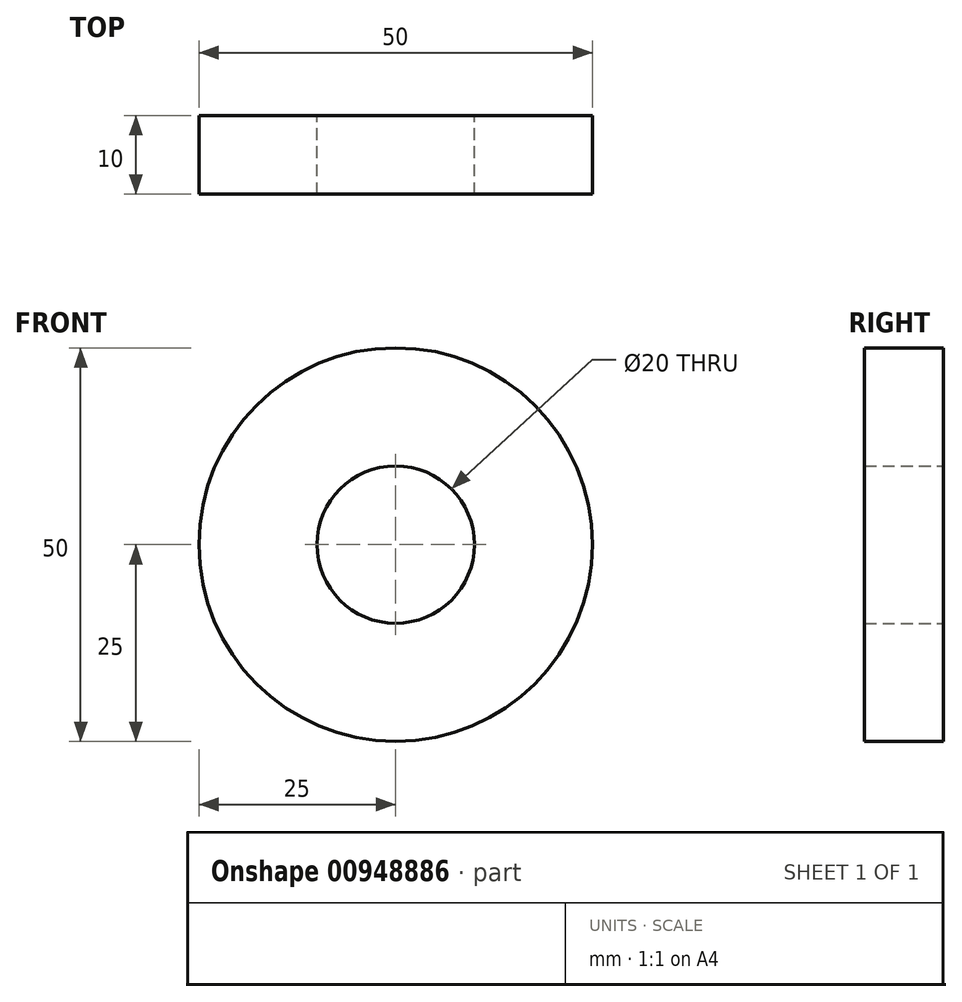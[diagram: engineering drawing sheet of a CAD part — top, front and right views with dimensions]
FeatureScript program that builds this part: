
annotation { "Feature Type Name" : "Feature", "Feature Type Description" : "" }
export const myFeature = defineFeature(function(context is Context, id is Id, definition is map)
    precondition{}
    {
        {
            var Q0;
            Q0=qCreatedBy(makeId("Front.planeOp"),FACE);
            var sketch = newSketch(context, id + "F0", { "sketchPlane" : qUnion([Q0])});
            skCircle(sketch, "E0", {"center": v(0, 0) * mm, "radius": 25 * mm});
            skCircle(sketch, "E1", {"center": v(0, 0) * mm, "radius": 10 * mm});
            skSolve(sketch);
        }
        {
            var Q0;
            Q0=qSketchRegion(id+"F0",true);
            extrude(context, id + "F1", {"entities" : qUnion([Q0]), "depth" : 10 * mm});
        }
    });
